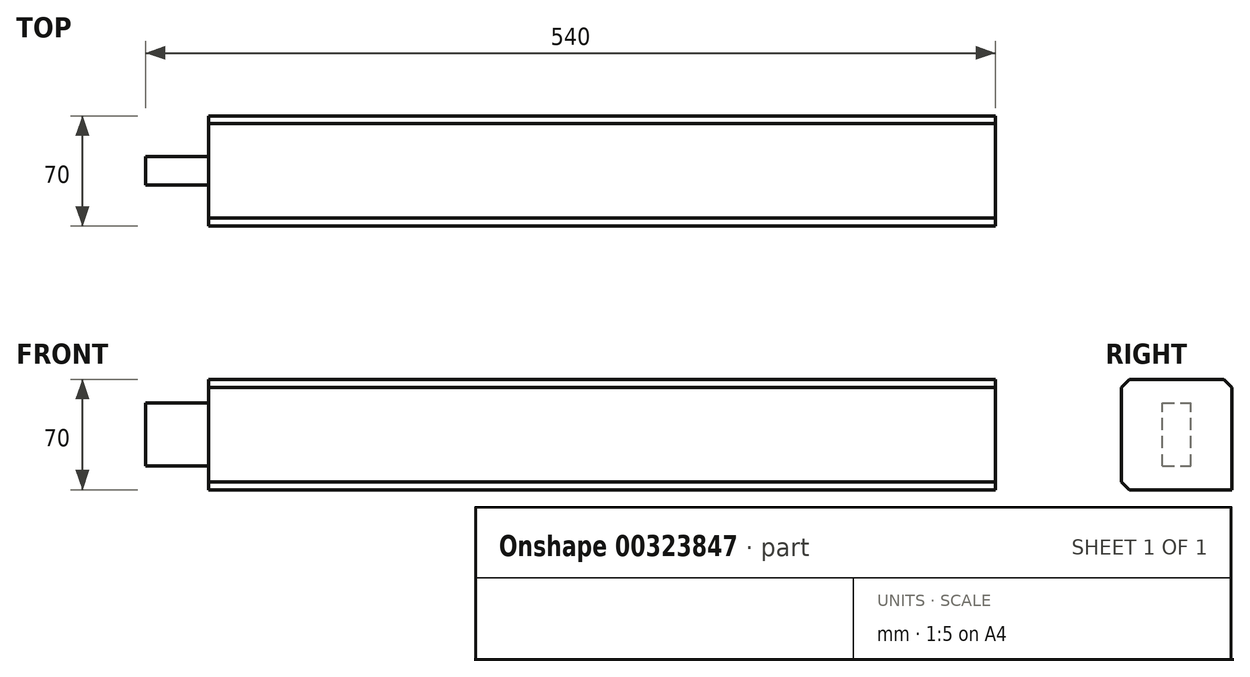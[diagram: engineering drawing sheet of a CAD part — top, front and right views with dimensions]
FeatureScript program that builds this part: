
annotation { "Feature Type Name" : "Feature", "Feature Type Description" : "" }
export const myFeature = defineFeature(function(context is Context, id is Id, definition is map)
    precondition{}
    {
        {
            var Q0;
            Q0=qCreatedBy(makeId("Right.planeOp"),FACE);
            var sketch = newSketch(context, id + "F0", { "sketchPlane" : qUnion([Q0])});
            skLineSegment(sketch, "E0.bottom", {"start": v(35, -35) * mm, "end": v(-35, -35) * mm});
            skLineSegment(sketch, "E0.top", {"start": v(35, 35) * mm, "end": v(-35, 35) * mm});
            skLineSegment(sketch, "E0.left", {"start": v(35, -35) * mm, "end": v(35, 35) * mm});
            skLineSegment(sketch, "E0.right", {"start": v(-35, -35) * mm, "end": v(-35, 35) * mm});
            skPoint(sketch, "E0.middle", {"position": v(0, 0) * mm});
            skSolve(sketch);
        }
        {
            var Q0;
            Q0 = qSketchRegion(id + "F0", true);
            extrude(context, id + "F1", {"entities" : qUnion([Q0]), "depth" : 500 * mm});
        }
        {
            var Q0;
            Q0=makeQuery(id+"F1.opExtrude","CAP_FACE",FACE,{"disambiguationData":[OSD([sQuery(id+"F0.wireOp",EDGE,"E0.bottom"),sQuery(id+"F0.wireOp",EDGE,"E0.top"),sQuery(id+"F0.wireOp",EDGE,"E0.left"),sQuery(id+"F0.wireOp",EDGE,"E0.right")])],"isStart":true});
            var sketch = newSketch(context, id + "F2", { "sketchPlane" : qUnion([Q0])});
            skLineSegment(sketch, "E1.bottom", {"start": v(9, -20) * mm, "end": v(-9, -20) * mm});
            skLineSegment(sketch, "E1.top", {"start": v(9, 20) * mm, "end": v(-9, 20) * mm});
            skLineSegment(sketch, "E1.left", {"start": v(9, -20) * mm, "end": v(9, 20) * mm});
            skLineSegment(sketch, "E1.right", {"start": v(-9, -20) * mm, "end": v(-9, 20) * mm});
            skPoint(sketch, "E1.middle", {"position": v(0, 0) * mm});
            skSolve(sketch);
        }
        {
            var Q0;
            Q0=makeQuery(id+"F2.imprint","IMPRINT",FACE,{"disambiguationData":[TD([[makeQuery(id+"F2.imprint","IMPRINT",EDGE,{"derivedFrom":sQuery(id+"F2.wireOp",EDGE,"E1.bottom")}),-1.0]])]});
            extrude(context, id + "F3", {"entities" : qUnion([Q0]), "operationType" : NewBodyOperationType.ADD, "depth" : 40 * mm});
        }
        {
            var Q0;
            Q0=makeQuery(id+"F1.opExtrude","SWEPT_EDGE",EDGE,{"disambiguationData":[OSD([sQuery(id+"F0.wireOp",EDGE,"E0.top"),sQuery(id+"F0.wireOp",EDGE,"E0.right")])]});
            var Q1;
            Q1=makeQuery(id+"F1.opExtrude","SWEPT_EDGE",EDGE,{"disambiguationData":[OSD([sQuery(id+"F0.wireOp",EDGE,"E0.top"),sQuery(id+"F0.wireOp",EDGE,"E0.left")])]});
            var Q2;
            Q2=makeQuery(id+"F1.opExtrude","SWEPT_EDGE",EDGE,{"disambiguationData":[OSD([sQuery(id+"F0.wireOp",EDGE,"E0.bottom"),sQuery(id+"F0.wireOp",EDGE,"E0.right")])]});
            chamfer(context, id + "F4", {"entities" : qUnion([Q0, Q1, Q2]), "width" : 5 * mm, "tangentPropagation" : true});
        }
    });
